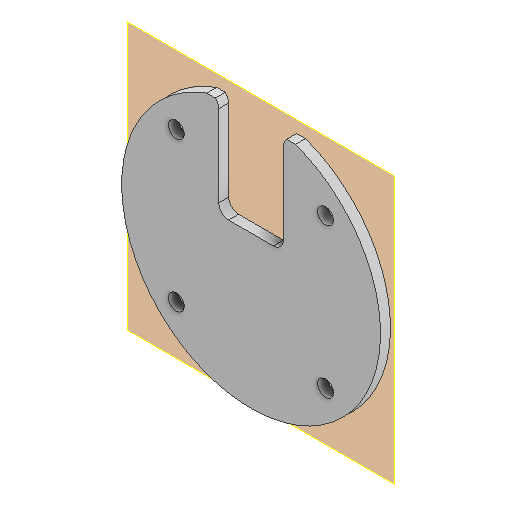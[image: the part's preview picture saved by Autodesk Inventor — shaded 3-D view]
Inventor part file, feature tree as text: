
AUTODESK INVENTOR PART (.ipt)
format: ipt  version: 2022 (Build 260153000, 153)  size: 148,480 bytes
history: native  units: mm
features: reference x6, plane x2, extrude x2, sketch x2, other x2, hole x1, fillet x1, projected_geometry x1
ambient origin geometry x8: Origin, YZ Plane, XZ Plane, XY Plane, X Axis, Y Axis, Z Axis, Center Point
bodies: Volumenkörper1 (feature_tree)
feature tree (17):
  plane  "Arbeitsebene1"
  extrude  "Extrusion1"  Depth=4.0mm
  plane  "Arbeitsebene2"
  hole  "Bohrung1"  [1 undecoded]
  extrude  "Extrusion2"  Depth=2.0mm
  fillet  "Rundung1"  [1 undecoded]
  sketch  "Skizze1"  dims[d0=4.0mm d1=4.0mm]
  reference  "Referenz1"
  sketch  "Skizze2"  dims[d2=2.0mm d3=0.0mm d4=3.2mm d5=6.0mm d6=4.0mm d7=2.0mm d8=90.0deg d9=8.0mm d10=20.594885mm d11=10.0mm d12=0.0mm d13=2.0mm]
  projected_geometry  "Projizierte Kontur1"
  reference  "Referenz2"
  reference  "Referenz3"
  reference  "Referenz4"
  reference  "Referenz5"
  reference  "Referenz6"
  other  "Assembly_Cube_SEEED_Xiao_Sense_Camera_v3.iam"
  other  "20_Cube_Insert_SEEED_Xiao_Sense_Camera:1"
note: 2 required parameter values undecoded (feature->parameter linkage not recoverable at this tier; creation-order binding heuristic only, values carry confidence <= 0.55)
